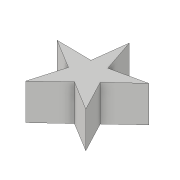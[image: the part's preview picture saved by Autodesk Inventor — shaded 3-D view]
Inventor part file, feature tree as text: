
AUTODESK INVENTOR PART (.ipt)
format: ipt  version: 2019 (Build 230136000, 136)  size: 82,432 bytes
history: native  units: in
note: dims shown in document units (in); Inventor stores cm internally (conversion verified against a paired STEP export)
features: extrude x1, sketch x1
ambient origin geometry x8: Origin, YZ Plane, XZ Plane, XY Plane, X Axis, Y Axis, Z Axis, Center Point
bodies: Solid1 (feature_tree)
feature tree (2):
  extrude  "Extrusion1"  Depth=4.7244in TaperAngle=0.0deg
  sketch  "Sketch1"  dims[d1=5.9055in d3=4.7244in d4=0.0in]
